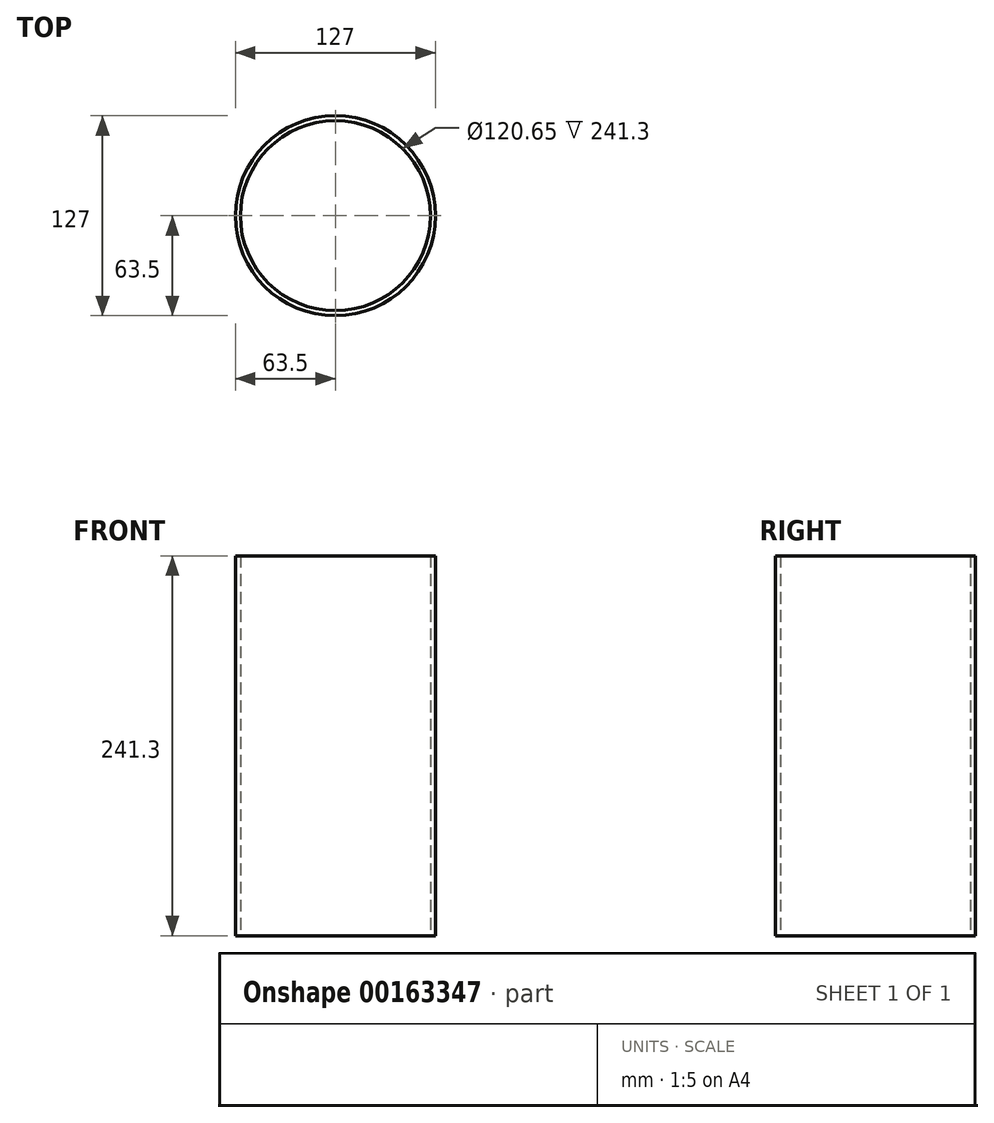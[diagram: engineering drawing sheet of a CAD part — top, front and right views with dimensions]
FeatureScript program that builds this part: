
annotation { "Feature Type Name" : "Feature", "Feature Type Description" : "" }
export const myFeature = defineFeature(function(context is Context, id is Id, definition is map)
    precondition{}
    {
        {
            var Q0;
            Q0=qCreatedBy(makeId("Top.planeOp"),FACE);
            var sketch = newSketch(context, id + "F0", { "sketchPlane" : qUnion([Q0])});
            skCircle(sketch, "E0", {"center": v(0, 0) * mm, "radius": 63.5 * mm});
            skCircle(sketch, "E1", {"center": v(0, 0) * mm, "radius": 60.33 * mm});
            skSolve(sketch);
        }
        {
            var Q0;
            Q0=makeQuery(id+"F0.imprint","IMPRINT",FACE,{"disambiguationData":[TD([[makeQuery(id+"F0.imprint","IMPRINT",EDGE,{"derivedFrom":sQuery(id+"F0.wireOp",EDGE,"E0")}),1.0]])]});
            extrude(context, id + "F1", {"entities" : qUnion([Q0]), "depth" : 241.3 * mm});
        }
    });
